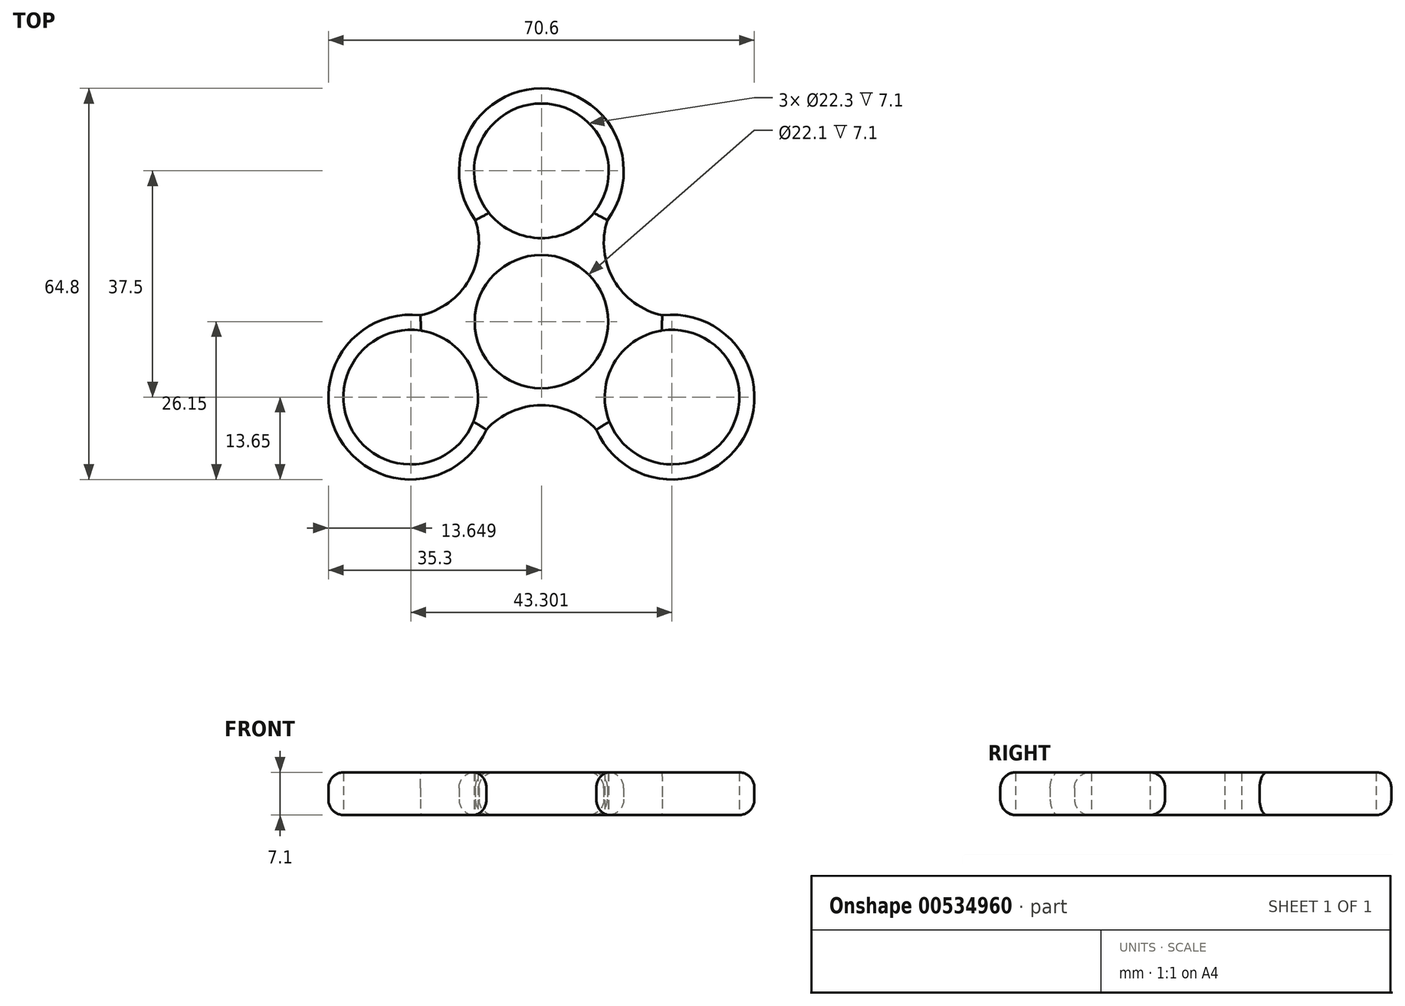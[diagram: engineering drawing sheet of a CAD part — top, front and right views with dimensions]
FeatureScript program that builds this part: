
annotation { "Feature Type Name" : "Feature", "Feature Type Description" : "" }
export const myFeature = defineFeature(function(context is Context, id is Id, definition is map)
    precondition{}
    {
        {
            var Q0;
            Q0=qCreatedBy(makeId("Top.planeOp"),FACE);
            var sketch = newSketch(context, id + "F0", { "sketchPlane" : qUnion([Q0])});
            skCircle(sketch, "E0", {"center": v(0, 0) * mm, "radius": 11.05 * mm});
            skCircle(sketch, "E1.cCircle", {"center": v(0, 0) * mm, "radius": 11.05 * mm, "construction": true});
            skLineSegment(sketch, "E1.0", {"start": v(0, 11.05) * mm, "end": v(9.57, -5.53) * mm});
            skLineSegment(sketch, "E1.1", {"start": v(9.57, -5.52) * mm, "end": v(-9.57, -5.53) * mm});
            skLineSegment(sketch, "E1.2", {"start": v(-9.57, -5.53) * mm, "end": v(0, 11.05) * mm});
            skLineSegment(sketch, "E2", {"start": v(0, 11.05) * mm, "end": v(0, 13.55) * mm});
            skLineSegment(sketch, "E3", {"start": v(9.57, -5.53) * mm, "end": v(12.04, -6.95) * mm});
            skLineSegment(sketch, "E4", {"start": v(-9.57, -5.52) * mm, "end": v(-12, -6.92) * mm});
            skCircle(sketch, "E5.0", {"center": v(0, 0) * mm, "radius": 13.85 * mm});
            skLineSegment(sketch, "E6", {"start": v(0, 13.55) * mm, "end": v(0, 25) * mm});
            skLineSegment(sketch, "E7", {"start": v(-12, -6.92) * mm, "end": v(-21.65, -12.5) * mm});
            skLineSegment(sketch, "E8", {"start": v(12.04, -6.95) * mm, "end": v(21.65, -12.5) * mm});
            skCircle(sketch, "E9", {"center": v(0, 25) * mm, "radius": 11.15 * mm});
            skCircle(sketch, "E10", {"center": v(21.65, -12.5) * mm, "radius": 11.15 * mm});
            skCircle(sketch, "E11", {"center": v(-21.65, -12.5) * mm, "radius": 11.15 * mm});
            skPoint(sketch, "E12", {"position": v(-4.78, 2.76) * mm});
            skCircle(sketch, "E13.0", {"center": v(0, 25) * mm, "radius": 13.65 * mm});
            skCircle(sketch, "E14.0", {"center": v(-21.65, -12.5) * mm, "radius": 13.65 * mm});
            skCircle(sketch, "E15.0", {"center": v(21.65, -12.5) * mm, "radius": 13.65 * mm});
            skLineSegment(sketch, "E16", {"start": v(0, 11.05) * mm, "end": v(0, -51.36) * mm});
            skPoint(sketch, "E16.endSnap0", {"position": v(0, -5.53) * mm});
            skLineSegment(sketch, "E17", {"start": v(-9.57, -5.53) * mm, "end": v(42.9, 24.76) * mm});
            skLineSegment(sketch, "E18", {"start": v(9.57, -5.52) * mm, "end": v(-42.6, 24.6) * mm});
            skPoint(sketch, "E19", {"position": v(4.78, 2.76) * mm});
            skLineSegment(sketch, "E20", {"start": v(11.82, 31.83) * mm, "end": v(33.47, -5.67) * mm});
            skCircle(sketch, "E21", {"center": v(22.65, 13.08) * mm, "radius": 12.3 * mm});
            skLineSegment(sketch, "E22", {"start": v(-11.82, 31.83) * mm, "end": v(-33.47, -5.68) * mm});
            skCircle(sketch, "E23", {"center": v(0, -26.14) * mm, "radius": 12.29 * mm});
            skCircle(sketch, "E24", {"center": v(-22.65, 13.07) * mm, "radius": 12.3 * mm});
            skLineSegment(sketch, "E25", {"start": v(21.65, -26.15) * mm, "end": v(-21.65, -26.15) * mm});
            skSolve(sketch);
        }
        {
            var Q0;
            {var subQ0=sQuery(id+"F0.wireOp",EDGE,"E9");Q0=makeQuery(id+"F0.imprint","IMPRINT",FACE,{"disambiguationData":[TD([[makeQuery(id+"F0.imprint","IMPRINT",EDGE,{"derivedFrom":subQ0}),-1.0]])]});}
            var Q1;
            {var subQ0=sQuery(id+"F0.wireOp",EDGE,"E24");var subQ1=sQuery(id+"F0.wireOp",EDGE,"E13.0");var subQ2=makeQuery(id+"F0.imprint","INTERSECT",VERTEX,{"disambiguationData":[OD(0.0)],"derivedFrom":[subQ1,subQ0]});Q1=makeQuery(id+"F0.imprint","IMPRINT",FACE,{"disambiguationData":[TD([[makeQuery(id+"F0.imprint","IMPRINT",EDGE,{"disambiguationData":[TD([[subQ2,-1.0]])],"derivedFrom":subQ1}),1.0]])]});}
            var Q2;
            {var subQ0=sQuery(id+"F0.wireOp",EDGE,"E21");var subQ1=sQuery(id+"F0.wireOp",EDGE,"E13.0");var subQ2=makeQuery(id+"F0.imprint","INTERSECT",VERTEX,{"disambiguationData":[OD(0.0)],"derivedFrom":[subQ1,subQ0]});Q2=makeQuery(id+"F0.imprint","IMPRINT",FACE,{"disambiguationData":[TD([[makeQuery(id+"F0.imprint","IMPRINT",EDGE,{"disambiguationData":[TD([[subQ2,-1.0]])],"derivedFrom":subQ1}),1.0]])]});}
            var Q3;
            {var subQ0=sQuery(id+"F0.wireOp",EDGE,"E2");Q3=makeQuery(id+"F0.imprint","IMPRINT",FACE,{"disambiguationData":[TD([[makeQuery(id+"F0.imprint","IMPRINT",EDGE,{"derivedFrom":subQ0}),-1.0]])]});}
            var Q4;
            {var subQ0=sQuery(id+"F0.wireOp",EDGE,"E2");Q4=makeQuery(id+"F0.imprint","IMPRINT",FACE,{"disambiguationData":[TD([[makeQuery(id+"F0.imprint","IMPRINT",EDGE,{"derivedFrom":subQ0}),1.0]])]});}
            var Q5;
            {var subQ0=sQuery(id+"F0.wireOp",EDGE,"E13.0");var subQ1=sQuery(id+"F0.wireOp",EDGE,"E5.0");var subQ2=makeQuery(id+"F0.imprint","INTERSECT",VERTEX,{"disambiguationData":[OD(0.0)],"derivedFrom":[subQ1,subQ0]});Q5=makeQuery(id+"F0.imprint","IMPRINT",FACE,{"disambiguationData":[TD([[makeQuery(id+"F0.imprint","IMPRINT",EDGE,{"disambiguationData":[TD([[subQ2,-1.0]])],"derivedFrom":subQ0}),-1.0]])]});}
            var Q6;
            {var subQ0=sQuery(id+"F0.wireOp",EDGE,"E13.0");var subQ1=sQuery(id+"F0.wireOp",EDGE,"E5.0");var subQ2=makeQuery(id+"F0.imprint","INTERSECT",VERTEX,{"disambiguationData":[OD(1.0)],"derivedFrom":[subQ1,subQ0]});Q6=makeQuery(id+"F0.imprint","IMPRINT",FACE,{"disambiguationData":[TD([[makeQuery(id+"F0.imprint","IMPRINT",EDGE,{"disambiguationData":[TD([[subQ2,1.0]])],"derivedFrom":subQ0}),-1.0]])]});}
            var Q7;
            {var subQ0=sQuery(id+"F0.wireOp",EDGE,"E13.0");var subQ5=sQuery(id+"F0.wireOp",EDGE,"E5.0");var subQ6=makeQuery(id+"F0.imprint","INTERSECT",VERTEX,{"disambiguationData":[OD(1.0)],"derivedFrom":[subQ5,subQ0]});Q7=makeQuery(id+"F0.imprint","IMPRINT",FACE,{"disambiguationData":[TD([[makeQuery(id+"F0.imprint","IMPRINT",EDGE,{"disambiguationData":[TD([[subQ6,-1.0]])],"derivedFrom":subQ5}),1.0]])]});}
            var Q8;
            {var subQ0=sQuery(id+"F0.wireOp",EDGE,"E13.0");var subQ5=sQuery(id+"F0.wireOp",EDGE,"E5.0");var subQ6=makeQuery(id+"F0.imprint","INTERSECT",VERTEX,{"disambiguationData":[OD(0.0)],"derivedFrom":[subQ5,subQ0]});Q8=makeQuery(id+"F0.imprint","IMPRINT",FACE,{"disambiguationData":[TD([[makeQuery(id+"F0.imprint","IMPRINT",EDGE,{"disambiguationData":[TD([[subQ6,1.0]])],"derivedFrom":subQ5}),1.0]])]});}
            var Q9;
            {var subQ3=sQuery(id+"F0.wireOp",EDGE,"E21");var subQ4=sQuery(id+"F0.wireOp",EDGE,"E5.0");var subQ9=makeQuery(id+"F0.imprint","INTERSECT",VERTEX,{"derivedFrom":[subQ4,subQ3]});Q9=makeQuery(id+"F0.imprint","IMPRINT",FACE,{"disambiguationData":[TD([[makeQuery(id+"F0.imprint","IMPRINT",EDGE,{"disambiguationData":[TD([[subQ9,1.0]])],"derivedFrom":subQ4}),1.0]])]});}
            var Q10;
            {var subQ0=sQuery(id+"F0.wireOp",EDGE,"E21");var subQ1=sQuery(id+"F0.wireOp",EDGE,"E5.0");var subQ2=makeQuery(id+"F0.imprint","INTERSECT",VERTEX,{"derivedFrom":[subQ1,subQ0]});Q10=makeQuery(id+"F0.imprint","IMPRINT",FACE,{"disambiguationData":[TD([[makeQuery(id+"F0.imprint","IMPRINT",EDGE,{"disambiguationData":[TD([[subQ2,1.0]])],"derivedFrom":subQ1}),-1.0]])]});}
            var Q11;
            {var subQ4=sQuery(id+"F0.wireOp",EDGE,"E10");Q11=makeQuery(id+"F0.imprint","IMPRINT",FACE,{"disambiguationData":[TD([[makeQuery(id+"F0.imprint","IMPRINT",EDGE,{"derivedFrom":subQ4}),-1.0]])]});}
            var Q12;
            {var subQ0=sQuery(id+"F0.wireOp",EDGE,"E15.0");var subQ1=sQuery(id+"F0.wireOp",EDGE,"E5.0");var subQ2=makeQuery(id+"F0.imprint","INTERSECT",VERTEX,{"disambiguationData":[OD(0.0)],"derivedFrom":[subQ1,subQ0]});Q12=makeQuery(id+"F0.imprint","IMPRINT",FACE,{"disambiguationData":[TD([[makeQuery(id+"F0.imprint","IMPRINT",EDGE,{"disambiguationData":[TD([[subQ2,-1.0]])],"derivedFrom":subQ0}),-1.0]])]});}
            var Q13;
            {var subQ0=sQuery(id+"F0.wireOp",EDGE,"E3");Q13=makeQuery(id+"F0.imprint","IMPRINT",FACE,{"disambiguationData":[TD([[makeQuery(id+"F0.imprint","IMPRINT",EDGE,{"derivedFrom":subQ0}),-1.0]])]});}
            var Q14;
            {var subQ0=sQuery(id+"F0.wireOp",EDGE,"E3");Q14=makeQuery(id+"F0.imprint","IMPRINT",FACE,{"disambiguationData":[TD([[makeQuery(id+"F0.imprint","IMPRINT",EDGE,{"derivedFrom":subQ0}),1.0]])]});}
            var Q15;
            {var subQ0=sQuery(id+"F0.wireOp",EDGE,"E15.0");var subQ5=sQuery(id+"F0.wireOp",EDGE,"E5.0");var subQ6=makeQuery(id+"F0.imprint","INTERSECT",VERTEX,{"disambiguationData":[OD(0.0)],"derivedFrom":[subQ5,subQ0]});Q15=makeQuery(id+"F0.imprint","IMPRINT",FACE,{"disambiguationData":[TD([[makeQuery(id+"F0.imprint","IMPRINT",EDGE,{"disambiguationData":[TD([[subQ6,1.0]])],"derivedFrom":subQ5}),1.0]])]});}
            var Q16;
            {var subQ0=sQuery(id+"F0.wireOp",EDGE,"E14.0");var subQ1=sQuery(id+"F0.wireOp",EDGE,"E4");var subQ2=makeQuery(id+"F0.imprint","INTERSECT",VERTEX,{"derivedFrom":[subQ1,subQ0]});Q16=makeQuery(id+"F0.imprint","IMPRINT",FACE,{"disambiguationData":[TD([[makeQuery(id+"F0.imprint","IMPRINT",EDGE,{"disambiguationData":[TD([[subQ2,1.0]])],"derivedFrom":subQ0}),-1.0]])]});}
            var Q17;
            {var subQ0=sQuery(id+"F0.wireOp",EDGE,"E14.0");var subQ1=sQuery(id+"F0.wireOp",EDGE,"E5.0");var subQ2=makeQuery(id+"F0.imprint","INTERSECT",VERTEX,{"disambiguationData":[OD(1.0)],"derivedFrom":[subQ1,subQ0]});Q17=makeQuery(id+"F0.imprint","IMPRINT",FACE,{"disambiguationData":[TD([[makeQuery(id+"F0.imprint","IMPRINT",EDGE,{"disambiguationData":[TD([[subQ2,1.0]])],"derivedFrom":subQ0}),-1.0]])]});}
            var Q18;
            Q18=makeQuery(id+"F0.imprint","IMPRINT",FACE,{"disambiguationData":[TD([[makeQuery(id+"F0.imprint","IMPRINT",EDGE,{"derivedFrom":sQuery(id+"F0.wireOp",EDGE,"E11")}),-1.0]])]});
            var Q19;
            {var subQ0=sQuery(id+"F0.wireOp",EDGE,"E5.0");var subQ1=sQuery(id+"F0.wireOp",EDGE,"E4");var subQ2=makeQuery(id+"F0.imprint","INTERSECT",VERTEX,{"derivedFrom":[subQ1,subQ0]});Q19=makeQuery(id+"F0.imprint","IMPRINT",FACE,{"disambiguationData":[TD([[makeQuery(id+"F0.imprint","IMPRINT",EDGE,{"disambiguationData":[TD([[subQ2,1.0]])],"derivedFrom":subQ1}),1.0]])]});}
            var Q20;
            {var subQ0=sQuery(id+"F0.wireOp",EDGE,"E5.0");var subQ1=sQuery(id+"F0.wireOp",EDGE,"E4");var subQ2=makeQuery(id+"F0.imprint","INTERSECT",VERTEX,{"derivedFrom":[subQ1,subQ0]});Q20=makeQuery(id+"F0.imprint","IMPRINT",FACE,{"disambiguationData":[TD([[makeQuery(id+"F0.imprint","IMPRINT",EDGE,{"disambiguationData":[TD([[subQ2,1.0]])],"derivedFrom":subQ1}),-1.0]])]});}
            var Q21;
            {var subQ0=sQuery(id+"F0.wireOp",EDGE,"E14.0");var subQ1=sQuery(id+"F0.wireOp",EDGE,"E5.0");var subQ2=makeQuery(id+"F0.imprint","INTERSECT",VERTEX,{"disambiguationData":[OD(0.0)],"derivedFrom":[subQ1,subQ0]});Q21=makeQuery(id+"F0.imprint","IMPRINT",FACE,{"disambiguationData":[TD([[makeQuery(id+"F0.imprint","IMPRINT",EDGE,{"disambiguationData":[TD([[subQ2,-1.0]])],"derivedFrom":subQ0}),-1.0]])]});}
            var Q22;
            {var subQ0=sQuery(id+"F0.wireOp",EDGE,"E14.0");var subQ5=sQuery(id+"F0.wireOp",EDGE,"E4");var subQ6=makeQuery(id+"F0.imprint","INTERSECT",VERTEX,{"derivedFrom":[subQ5,subQ0]});Q22=makeQuery(id+"F0.imprint","IMPRINT",FACE,{"disambiguationData":[TD([[makeQuery(id+"F0.imprint","IMPRINT",EDGE,{"disambiguationData":[TD([[subQ6,-1.0]])],"derivedFrom":subQ0}),-1.0]])]});}
            var Q23;
            {var subQ0=sQuery(id+"F0.wireOp",EDGE,"E21");var subQ1=sQuery(id+"F0.wireOp",EDGE,"E15.0");var subQ2=makeQuery(id+"F0.imprint","INTERSECT",VERTEX,{"disambiguationData":[OD(0.0)],"derivedFrom":[subQ1,subQ0]});Q23=makeQuery(id+"F0.imprint","IMPRINT",FACE,{"disambiguationData":[TD([[makeQuery(id+"F0.imprint","IMPRINT",EDGE,{"disambiguationData":[TD([[subQ2,-1.0]])],"derivedFrom":subQ1}),1.0]])]});}
            var Q24;
            {var subQ0=sQuery(id+"F0.wireOp",EDGE,"E23");var subQ1=sQuery(id+"F0.wireOp",EDGE,"E15.0");var subQ2=makeQuery(id+"F0.imprint","INTERSECT",VERTEX,{"disambiguationData":[OD(0.0)],"derivedFrom":[subQ1,subQ0]});Q24=makeQuery(id+"F0.imprint","IMPRINT",FACE,{"disambiguationData":[TD([[makeQuery(id+"F0.imprint","IMPRINT",EDGE,{"disambiguationData":[TD([[subQ2,-1.0]])],"derivedFrom":subQ1}),1.0]])]});}
            var Q25;
            {var subQ0=sQuery(id+"F0.wireOp",EDGE,"E24");var subQ1=sQuery(id+"F0.wireOp",EDGE,"E14.0");var subQ2=makeQuery(id+"F0.imprint","INTERSECT",VERTEX,{"disambiguationData":[OD(0.0)],"derivedFrom":[subQ1,subQ0]});Q25=makeQuery(id+"F0.imprint","IMPRINT",FACE,{"disambiguationData":[TD([[makeQuery(id+"F0.imprint","IMPRINT",EDGE,{"disambiguationData":[TD([[subQ2,-1.0]])],"derivedFrom":subQ1}),1.0]])]});}
            var Q26;
            {var subQ0=sQuery(id+"F0.wireOp",EDGE,"E23");var subQ1=sQuery(id+"F0.wireOp",EDGE,"E14.0");var subQ2=makeQuery(id+"F0.imprint","INTERSECT",VERTEX,{"disambiguationData":[OD(0.0)],"derivedFrom":[subQ1,subQ0]});Q26=makeQuery(id+"F0.imprint","IMPRINT",FACE,{"disambiguationData":[TD([[makeQuery(id+"F0.imprint","IMPRINT",EDGE,{"disambiguationData":[TD([[subQ2,-1.0]])],"derivedFrom":subQ1}),1.0]])]});}
            var Q27;
            {var subQ0=sQuery(id+"F0.wireOp",EDGE,"E15.0");var subQ5=sQuery(id+"F0.wireOp",EDGE,"E5.0");var subQ6=makeQuery(id+"F0.imprint","INTERSECT",VERTEX,{"disambiguationData":[OD(1.0)],"derivedFrom":[subQ5,subQ0]});Q27=makeQuery(id+"F0.imprint","IMPRINT",FACE,{"disambiguationData":[TD([[makeQuery(id+"F0.imprint","IMPRINT",EDGE,{"disambiguationData":[TD([[subQ6,-1.0]])],"derivedFrom":subQ5}),1.0]])]});}
            var Q28;
            {var subQ0=sQuery(id+"F0.wireOp",EDGE,"E15.0");var subQ1=sQuery(id+"F0.wireOp",EDGE,"E5.0");var subQ2=makeQuery(id+"F0.imprint","INTERSECT",VERTEX,{"disambiguationData":[OD(1.0)],"derivedFrom":[subQ1,subQ0]});Q28=makeQuery(id+"F0.imprint","IMPRINT",FACE,{"disambiguationData":[TD([[makeQuery(id+"F0.imprint","IMPRINT",EDGE,{"disambiguationData":[TD([[subQ2,1.0]])],"derivedFrom":subQ0}),-1.0]])]});}
            extrude(context, id + "F1", {"entities" : qUnion([Q0, Q1, Q2, Q3, Q4, Q5, Q6, Q7, Q8, Q9, Q10, Q11, Q12, Q13, Q14, Q15, Q16, Q17, Q18, Q19, Q20, Q21, Q22, Q23, Q24, Q25, Q26, Q27, Q28]), "depth" : 7.1 * mm, "offsetDistance" : 25 * mm});
        }
        {
            var Q0;
            Q0=makeQuery(id+"F1.opExtrude","CAP_EDGE",EDGE,{"disambiguationData":[OSD([sQuery(id+"F0.wireOp",EDGE,"E23")])],"isStart":false});
            var Q1;
            Q1=makeQuery(id+"F1.opExtrude","CAP_EDGE",EDGE,{"disambiguationData":[OSD([sQuery(id+"F0.wireOp",EDGE,"E14.0")])],"isStart":false});
            var Q2;
            Q2=makeQuery(id+"F1.opExtrude","CAP_EDGE",EDGE,{"disambiguationData":[OSD([sQuery(id+"F0.wireOp",EDGE,"E15.0")])],"isStart":false});
            var Q3;
            Q3=makeQuery(id+"F1.opExtrude","CAP_EDGE",EDGE,{"disambiguationData":[OSD([sQuery(id+"F0.wireOp",EDGE,"E21")])],"isStart":false});
            var Q4;
            Q4=makeQuery(id+"F1.opExtrude","CAP_EDGE",EDGE,{"disambiguationData":[OSD([sQuery(id+"F0.wireOp",EDGE,"E24")])],"isStart":false});
            var Q5;
            Q5=makeQuery(id+"F1.opExtrude","CAP_EDGE",EDGE,{"disambiguationData":[OSD([sQuery(id+"F0.wireOp",EDGE,"E13.0")])],"isStart":false});
            var Q6;
            Q6=makeQuery(id+"F1.opExtrude","CAP_EDGE",EDGE,{"disambiguationData":[OSD([sQuery(id+"F0.wireOp",EDGE,"E13.0")])],"isStart":true});
            var Q7;
            Q7=makeQuery(id+"F1.opExtrude","CAP_EDGE",EDGE,{"disambiguationData":[OSD([sQuery(id+"F0.wireOp",EDGE,"E24")])],"isStart":true});
            var Q8;
            Q8=makeQuery(id+"F1.opExtrude","CAP_EDGE",EDGE,{"disambiguationData":[OSD([sQuery(id+"F0.wireOp",EDGE,"E14.0")])],"isStart":true});
            var Q9;
            Q9=makeQuery(id+"F1.opExtrude","CAP_EDGE",EDGE,{"disambiguationData":[OSD([sQuery(id+"F0.wireOp",EDGE,"E23")])],"isStart":true});
            var Q10;
            Q10=makeQuery(id+"F1.opExtrude","CAP_EDGE",EDGE,{"disambiguationData":[OSD([sQuery(id+"F0.wireOp",EDGE,"E15.0")])],"isStart":true});
            var Q11;
            Q11=makeQuery(id+"F1.opExtrude","CAP_EDGE",EDGE,{"disambiguationData":[OSD([sQuery(id+"F0.wireOp",EDGE,"E21")])],"isStart":true});
            fillet(context, id + "F2", {"entities" : qUnion([Q0, Q1, Q2, Q3, Q4, Q5, Q6, Q7, Q8, Q9, Q10, Q11]), "radius" : 2.6 * mm, "tangentPropagation" : true, "allowEdgeOverflow" : false});
        }
    });
